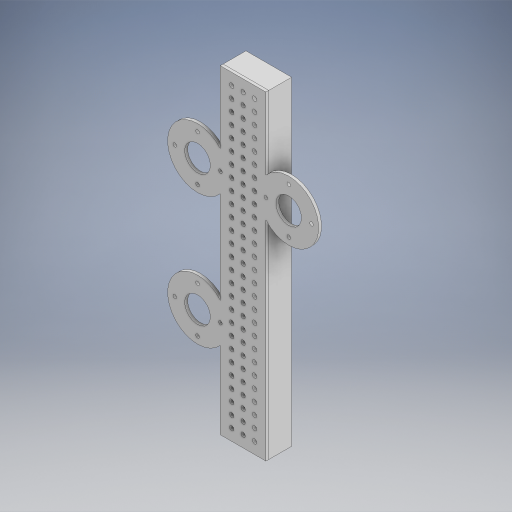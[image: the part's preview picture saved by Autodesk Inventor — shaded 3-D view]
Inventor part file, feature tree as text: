
AUTODESK INVENTOR PART (.ipt)
format: ipt  version: 2024.2 (Build 282272000, 272)  size: 609,792 bytes
history: native  units: in
note: dims shown in document units (in); Inventor stores cm internally (conversion verified against a paired STEP export)
features: extrude x3, sketch x3, projected_geometry x1
ambient origin geometry x8: Origin, YZ Plane, XZ Plane, XY Plane, X Axis, Y Axis, Z Axis, Center Point
bodies: Solid1 (feature_tree), Solid2 (feature_tree)
feature tree (7):
  extrude  "Extrusion1"  Depth=1.0in
  extrude  "Extrusion2"  Depth=14.0in
  extrude  "Extrusion3"  Depth=0.125in
  sketch  "Sketch1"  dims[d0=2.0in d1=1.0in]
  sketch  "Sketch2"  dims[d2=14.0in d3=0.0in d4=0.196in]
  sketch  "Sketch3"  dims[d5=0.5in d6=0.5in d7=1.1811in d9=0.5in d10=10.6299in d12=0.5in d15=14.0in d16=0.0in d17=1.124in d18=4.0in d19=1.124in d20=4.0in d21=3.991in d22=0.994in d23=1.124in d24=5.75in d25=0.159in d26=0.159in d27=2.0in d28=1.0in d29=1.5748in d31=270.0deg d33=1.0in d34=1.5748in d36=360.0deg d38=0.159in d39=1.0in d40=1.5748in d42=360.0deg d44=0.75in d45=0.75in d46=0.75in d47=0.5in d48=1.0in d49=0.5in d50=1.0in d51=0.5in d52=1.0in d53=0.5in d54=1.0in d56=1.0in d57=0.5in d58=1.0in d59=0.125in d60=0.0in]
  projected_geometry  "Projected Loop1"
